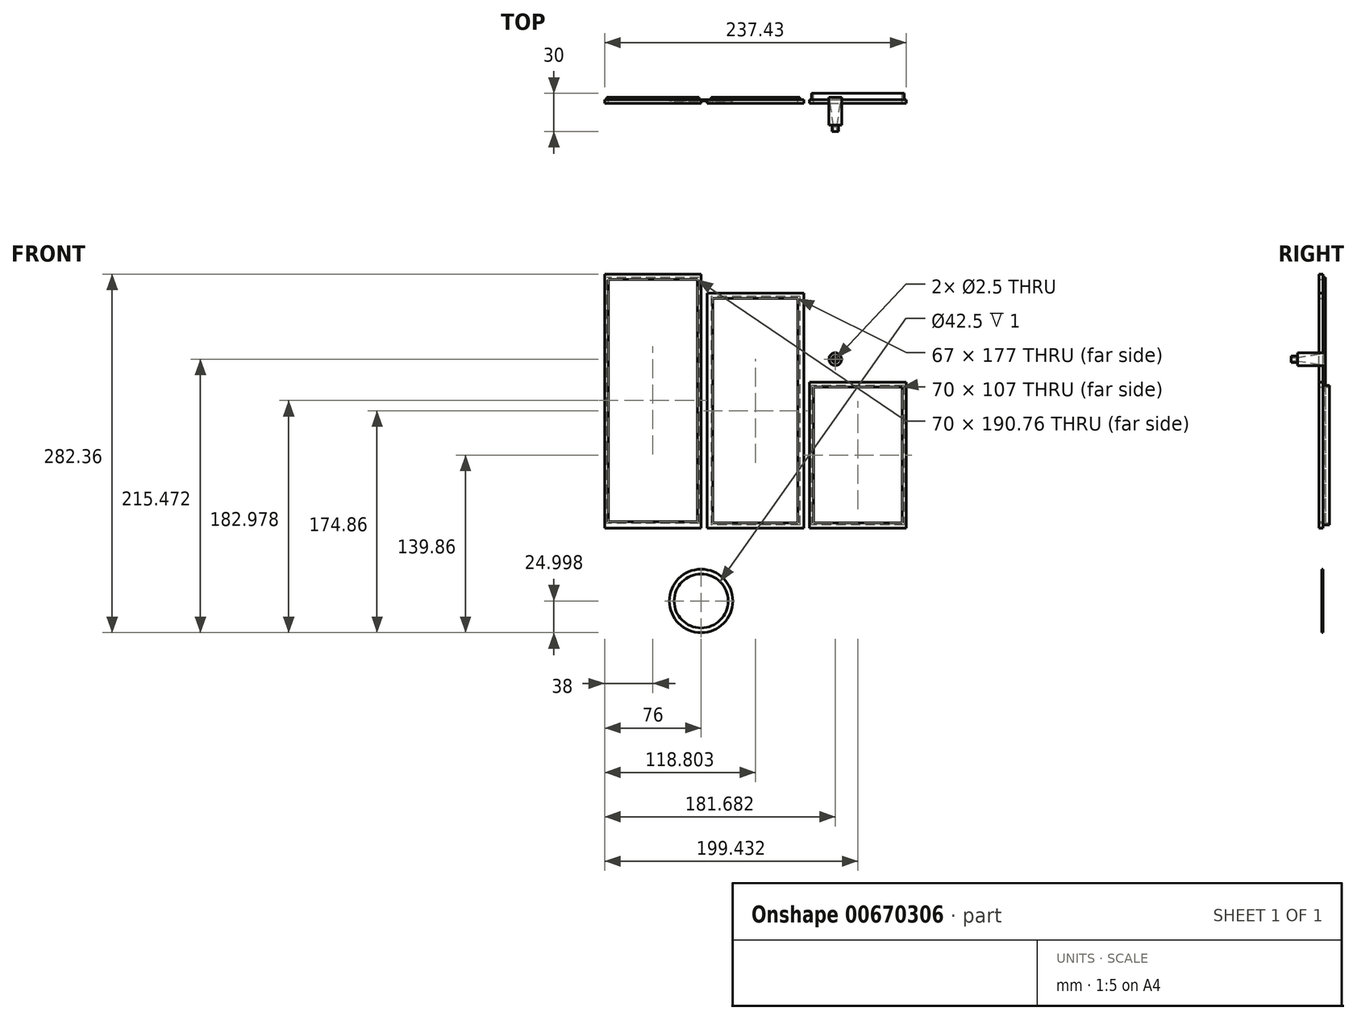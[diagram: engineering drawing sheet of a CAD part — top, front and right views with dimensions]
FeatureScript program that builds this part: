
annotation { "Feature Type Name" : "Feature", "Feature Type Description" : "" }
export const myFeature = defineFeature(function(context is Context, id is Id, definition is map)
    precondition{}
    {
        {
            var Q0;
            Q0=qCreatedBy(makeId("Front.planeOp"),FACE);
            var sketch = newSketch(context, id + "F0", { "sketchPlane" : qUnion([Q0])});
            skLineSegment(sketch, "E0.bottom", {"start": v(0, 0) * mm, "end": v(-76, 0) * mm});
            skLineSegment(sketch, "E0.top", {"start": v(0, 200) * mm, "end": v(-76, 200) * mm});
            skLineSegment(sketch, "E0.left", {"start": v(0, 0) * mm, "end": v(0, 200) * mm});
            skLineSegment(sketch, "E0.right", {"start": v(-76, 0) * mm, "end": v(-76, 200) * mm});
            skSolve(sketch);
        }
        {
            var Q0;
            Q0 = qSketchRegion(id + "F0", true);
            extrude(context, id + "F1", {"entities" : qUnion([Q0]), "depth" : 3 * mm, "offsetDistance" : 25.4 * mm});
        }
        {
            var Q0;
            Q0=makeQuery(id+"F1.opExtrude","CAP_FACE",FACE,{"disambiguationData":[OSD([sQuery(id+"F0.wireOp",EDGE,"E0.bottom"),sQuery(id+"F0.wireOp",EDGE,"E0.top"),sQuery(id+"F0.wireOp",EDGE,"E0.left"),sQuery(id+"F0.wireOp",EDGE,"E0.right")])],"isStart":true});
            var sketch = newSketch(context, id + "F2", { "sketchPlane" : qUnion([Q0])});
            skLineSegment(sketch, "E1", {"start": v(0, 0) * mm, "end": v(0, 3.74) * mm});
            skLineSegment(sketch, "E2", {"start": v(0, 0) * mm, "end": v(1.5, 0) * mm});
            skLineSegment(sketch, "E3", {"start": v(76, 200) * mm, "end": v(74.5, 200) * mm});
            skLineSegment(sketch, "E4", {"start": v(74.5, 200) * mm, "end": v(74.5, 197.5) * mm});
            skLineSegment(sketch, "E5.bottom", {"start": v(1.5, 3.74) * mm, "end": v(74.5, 3.74) * mm});
            skLineSegment(sketch, "E5.top", {"start": v(1.5, 197.5) * mm, "end": v(74.5, 197.5) * mm});
            skLineSegment(sketch, "E5.left", {"start": v(1.5, 3.74) * mm, "end": v(1.5, 197.5) * mm});
            skLineSegment(sketch, "E5.right", {"start": v(74.5, 3.74) * mm, "end": v(74.5, 197.5) * mm});
            skSolve(sketch);
        }
        {
            var Q0;
            Q0 = qSketchRegion(id + "F2", true);
            extrude(context, id + "F3", {"entities" : qUnion([Q0]), "operationType" : NewBodyOperationType.ADD, "depth" : 2 * mm, "offsetDistance" : 25.4 * mm});
        }
        {
            var Q0;
            Q0=makeQuery(id+"F3.opExtrude","CAP_FACE",FACE,{"disambiguationData":[OSD([sQuery(id+"F2.wireOp",EDGE,"E5.bottom"),sQuery(id+"F2.wireOp",EDGE,"E5.top"),sQuery(id+"F2.wireOp",EDGE,"E5.left"),sQuery(id+"F2.wireOp",EDGE,"E5.right")])],"isStart":false});
            var sketch = newSketch(context, id + "F4", { "sketchPlane" : qUnion([Q0])});
            skLineSegment(sketch, "E6", {"start": v(74.5, 3.74) * mm, "end": v(73, 3.74) * mm});
            skLineSegment(sketch, "E7", {"start": v(73, 3.74) * mm, "end": v(73, 5.24) * mm});
            skLineSegment(sketch, "E8", {"start": v(1.5, 197.5) * mm, "end": v(3, 197.5) * mm});
            skLineSegment(sketch, "E9", {"start": v(3, 197.5) * mm, "end": v(3, 196) * mm});
            skLineSegment(sketch, "E10.bottom", {"start": v(3, 196) * mm, "end": v(73, 196) * mm});
            skLineSegment(sketch, "E10.top", {"start": v(3, 5.24) * mm, "end": v(73, 5.24) * mm});
            skLineSegment(sketch, "E10.left", {"start": v(3, 196) * mm, "end": v(3, 5.24) * mm});
            skLineSegment(sketch, "E10.right", {"start": v(73, 196) * mm, "end": v(73, 5.24) * mm});
            skSolve(sketch);
        }
        {
            var Q0;
            Q0 = qSketchRegion(id + "F4", true);
            extrude(context, id + "F5", {"entities" : qUnion([Q0]), "operationType" : NewBodyOperationType.REMOVE, "oppositeDirection" : true, "depth" : 25.4 * mm, "offsetDistance" : 25.4 * mm});
        }
        {
            var Q0;
            Q0=qCreatedBy(makeId("Front.planeOp"),FACE);
            var sketch = newSketch(context, id + "F6", { "sketchPlane" : qUnion([Q0])});
            skLineSegment(sketch, "E11.bottom", {"start": v(4.8, 0) * mm, "end": v(80.8, 0) * mm});
            skLineSegment(sketch, "E11.top", {"start": v(4.8, 185) * mm, "end": v(80.8, 185) * mm});
            skLineSegment(sketch, "E11.left", {"start": v(4.8, 0) * mm, "end": v(4.8, 185) * mm});
            skLineSegment(sketch, "E11.right", {"start": v(80.8, 0) * mm, "end": v(80.8, 185) * mm});
            skSolve(sketch);
        }
        {
            var Q0;
            Q0 = qSketchRegion(id + "F6", true);
            extrude(context, id + "F7", {"entities" : qUnion([Q0]), "depth" : 3 * mm, "offsetDistance" : 25.4 * mm});
        }
        {
            var Q0;
            Q0=makeQuery(id+"F7.opExtrude","CAP_FACE",FACE,{"disambiguationData":[OSD([sQuery(id+"F6.wireOp",EDGE,"E11.bottom"),sQuery(id+"F6.wireOp",EDGE,"E11.top"),sQuery(id+"F6.wireOp",EDGE,"E11.left"),sQuery(id+"F6.wireOp",EDGE,"E11.right")])],"isStart":true});
            var sketch = newSketch(context, id + "F8", { "sketchPlane" : qUnion([Q0])});
            skLineSegment(sketch, "E12.bottom", {"start": v(-4.8, 0) * mm, "end": v(-7.8, 0) * mm});
            skLineSegment(sketch, "E12.top", {"start": v(-4.8, 2.5) * mm, "end": v(-7.8, 2.5) * mm});
            skLineSegment(sketch, "E12.left", {"start": v(-4.8, 0) * mm, "end": v(-4.8, 2.5) * mm});
            skLineSegment(sketch, "E12.right", {"start": v(-7.8, 0) * mm, "end": v(-7.8, 2.5) * mm});
            skLineSegment(sketch, "E13.bottom", {"start": v(-80.8, 185) * mm, "end": v(-77.8, 185) * mm});
            skLineSegment(sketch, "E13.top", {"start": v(-80.8, 182.5) * mm, "end": v(-77.8, 182.5) * mm});
            skLineSegment(sketch, "E13.left", {"start": v(-80.8, 185) * mm, "end": v(-80.8, 182.5) * mm});
            skLineSegment(sketch, "E13.right", {"start": v(-77.8, 185) * mm, "end": v(-77.8, 182.5) * mm});
            skLineSegment(sketch, "E14.bottom", {"start": v(-77.8, 182.5) * mm, "end": v(-7.8, 182.5) * mm});
            skLineSegment(sketch, "E14.top", {"start": v(-77.8, 2.5) * mm, "end": v(-7.8, 2.5) * mm});
            skLineSegment(sketch, "E14.left", {"start": v(-77.8, 182.5) * mm, "end": v(-77.8, 2.5) * mm});
            skLineSegment(sketch, "E14.right", {"start": v(-7.8, 182.5) * mm, "end": v(-7.8, 2.5) * mm});
            skSolve(sketch);
        }
        {
            var Q0;
            Q0=makeQuery(id+"F8.imprint","IMPRINT",FACE,{"disambiguationData":[TD([[makeQuery(id+"F8.imprint","IMPRINT",EDGE,{"derivedFrom":sQuery(id+"F8.wireOp",EDGE,"E14.bottom")}),-1.0]])]});
            extrude(context, id + "F9", {"entities" : qUnion([Q0]), "operationType" : NewBodyOperationType.ADD, "depth" : 2 * mm, "offsetDistance" : 25.4 * mm});
        }
        {
            var Q0;
            Q0=makeQuery(id+"F9.opExtrude","CAP_FACE",FACE,{"disambiguationData":[OSD([sQuery(id+"F8.wireOp",EDGE,"E14.bottom"),sQuery(id+"F8.wireOp",EDGE,"E14.top"),sQuery(id+"F8.wireOp",EDGE,"E14.left"),sQuery(id+"F8.wireOp",EDGE,"E14.right")])],"isStart":false});
            var sketch = newSketch(context, id + "F10", { "sketchPlane" : qUnion([Q0])});
            skLineSegment(sketch, "E15.bottom", {"start": v(-77.8, 182.5) * mm, "end": v(-76.3, 182.5) * mm});
            skLineSegment(sketch, "E15.top", {"start": v(-77.8, 181) * mm, "end": v(-76.3, 181) * mm});
            skLineSegment(sketch, "E15.left", {"start": v(-77.8, 182.5) * mm, "end": v(-77.8, 181) * mm});
            skLineSegment(sketch, "E15.right", {"start": v(-76.3, 182.5) * mm, "end": v(-76.3, 181) * mm});
            skLineSegment(sketch, "E16.bottom", {"start": v(-7.8, 2.5) * mm, "end": v(-9.3, 2.5) * mm});
            skLineSegment(sketch, "E16.top", {"start": v(-7.8, 4) * mm, "end": v(-9.3, 4) * mm});
            skLineSegment(sketch, "E16.left", {"start": v(-7.8, 2.5) * mm, "end": v(-7.8, 4) * mm});
            skLineSegment(sketch, "E16.right", {"start": v(-9.3, 2.5) * mm, "end": v(-9.3, 4) * mm});
            skLineSegment(sketch, "E17.bottom", {"start": v(-9.3, 4) * mm, "end": v(-76.3, 4) * mm});
            skLineSegment(sketch, "E17.top", {"start": v(-9.3, 181) * mm, "end": v(-76.3, 181) * mm});
            skLineSegment(sketch, "E17.left", {"start": v(-9.3, 4) * mm, "end": v(-9.3, 181) * mm});
            skLineSegment(sketch, "E17.right", {"start": v(-76.3, 4) * mm, "end": v(-76.3, 181) * mm});
            skSolve(sketch);
        }
        {
            var Q0;
            Q0=makeQuery(id+"F10.imprint","IMPRINT",FACE,{"disambiguationData":[TD([[makeQuery(id+"F10.imprint","IMPRINT",EDGE,{"derivedFrom":sQuery(id+"F10.wireOp",EDGE,"E17.bottom")}),-1.0]])]});
            extrude(context, id + "F11", {"entities" : qUnion([Q0]), "operationType" : NewBodyOperationType.REMOVE, "oppositeDirection" : true, "depth" : 25.4 * mm, "offsetDistance" : 25.4 * mm});
        }
        {
            var Q0;
            Q0=qCreatedBy(makeId("Front.planeOp"),FACE);
            var sketch = newSketch(context, id + "F12", { "sketchPlane" : qUnion([Q0])});
            skLineSegment(sketch, "E18.bottom", {"start": v(85.43, 0) * mm, "end": v(161.43, 0) * mm});
            skLineSegment(sketch, "E18.top", {"start": v(85.43, 115) * mm, "end": v(161.43, 115) * mm});
            skLineSegment(sketch, "E18.left", {"start": v(85.43, 0) * mm, "end": v(85.43, 115) * mm});
            skLineSegment(sketch, "E18.right", {"start": v(161.43, 0) * mm, "end": v(161.43, 115) * mm});
            skSolve(sketch);
        }
        {
            var Q0;
            Q0 = qSketchRegion(id + "F12", true);
            extrude(context, id + "F13", {"entities" : qUnion([Q0]), "depth" : 3 * mm, "offsetDistance" : 25.4 * mm});
        }
        {
            var Q0;
            Q0=makeQuery(id+"F13.opExtrude","CAP_FACE",FACE,{"disambiguationData":[OSD([sQuery(id+"F12.wireOp",EDGE,"E18.bottom"),sQuery(id+"F12.wireOp",EDGE,"E18.top"),sQuery(id+"F12.wireOp",EDGE,"E18.left"),sQuery(id+"F12.wireOp",EDGE,"E18.right")])],"isStart":true});
            var sketch = newSketch(context, id + "F14", { "sketchPlane" : qUnion([Q0])});
            skLineSegment(sketch, "E19.bottom", {"start": v(-85.43, 0) * mm, "end": v(-86.93, 0) * mm});
            skLineSegment(sketch, "E19.top", {"start": v(-85.43, 2.5) * mm, "end": v(-86.93, 2.5) * mm});
            skLineSegment(sketch, "E19.left", {"start": v(-85.43, 0) * mm, "end": v(-85.43, 2.5) * mm});
            skLineSegment(sketch, "E19.right", {"start": v(-86.93, 0) * mm, "end": v(-86.93, 2.5) * mm});
            skLineSegment(sketch, "E20.bottom", {"start": v(-161.43, 115) * mm, "end": v(-159.93, 115) * mm});
            skLineSegment(sketch, "E20.top", {"start": v(-161.43, 112.5) * mm, "end": v(-159.93, 112.5) * mm});
            skLineSegment(sketch, "E20.left", {"start": v(-161.43, 115) * mm, "end": v(-161.43, 112.5) * mm});
            skLineSegment(sketch, "E20.right", {"start": v(-159.93, 115) * mm, "end": v(-159.93, 112.5) * mm});
            skLineSegment(sketch, "E21.bottom", {"start": v(-159.93, 112.5) * mm, "end": v(-86.93, 112.5) * mm});
            skLineSegment(sketch, "E21.top", {"start": v(-159.93, 2.5) * mm, "end": v(-86.93, 2.5) * mm});
            skLineSegment(sketch, "E21.left", {"start": v(-159.93, 112.5) * mm, "end": v(-159.93, 2.5) * mm});
            skLineSegment(sketch, "E21.right", {"start": v(-86.93, 112.5) * mm, "end": v(-86.93, 2.5) * mm});
            skSolve(sketch);
        }
        {
            var Q0;
            Q0=makeQuery(id+"F14.imprint","IMPRINT",FACE,{"disambiguationData":[TD([[makeQuery(id+"F14.imprint","IMPRINT",EDGE,{"derivedFrom":sQuery(id+"F14.wireOp",EDGE,"E21.bottom")}),-1.0]])]});
            extrude(context, id + "F15", {"entities" : qUnion([Q0]), "operationType" : NewBodyOperationType.ADD, "depth" : 5 * mm, "offsetDistance" : 25.4 * mm});
        }
        {
            var Q0;
            Q0=makeQuery(id+"F15.opExtrude","CAP_FACE",FACE,{"disambiguationData":[OSD([sQuery(id+"F14.wireOp",EDGE,"E21.bottom"),sQuery(id+"F14.wireOp",EDGE,"E21.top"),sQuery(id+"F14.wireOp",EDGE,"E21.left"),sQuery(id+"F14.wireOp",EDGE,"E21.right")])],"isStart":false});
            var sketch = newSketch(context, id + "F16", { "sketchPlane" : qUnion([Q0])});
            skLineSegment(sketch, "E22.bottom", {"start": v(-86.93, 2.5) * mm, "end": v(-88.43, 2.5) * mm});
            skLineSegment(sketch, "E22.top", {"start": v(-86.93, 4) * mm, "end": v(-88.43, 4) * mm});
            skLineSegment(sketch, "E22.left", {"start": v(-86.93, 2.5) * mm, "end": v(-86.93, 4) * mm});
            skLineSegment(sketch, "E22.right", {"start": v(-88.43, 2.5) * mm, "end": v(-88.43, 4) * mm});
            skLineSegment(sketch, "E23.bottom", {"start": v(-159.93, 112.5) * mm, "end": v(-158.43, 112.5) * mm});
            skLineSegment(sketch, "E23.top", {"start": v(-159.93, 111) * mm, "end": v(-158.43, 111) * mm});
            skLineSegment(sketch, "E23.left", {"start": v(-159.93, 112.5) * mm, "end": v(-159.93, 111) * mm});
            skLineSegment(sketch, "E23.right", {"start": v(-158.43, 112.5) * mm, "end": v(-158.43, 111) * mm});
            skLineSegment(sketch, "E24.bottom", {"start": v(-158.43, 111) * mm, "end": v(-88.43, 111) * mm});
            skLineSegment(sketch, "E24.top", {"start": v(-158.43, 4) * mm, "end": v(-88.43, 4) * mm});
            skLineSegment(sketch, "E24.left", {"start": v(-158.43, 111) * mm, "end": v(-158.43, 4) * mm});
            skLineSegment(sketch, "E24.right", {"start": v(-88.43, 111) * mm, "end": v(-88.43, 4) * mm});
            skSolve(sketch);
        }
        {
            var Q0;
            Q0=makeQuery(id+"F16.imprint","IMPRINT",FACE,{"disambiguationData":[TD([[makeQuery(id+"F16.imprint","IMPRINT",EDGE,{"derivedFrom":sQuery(id+"F16.wireOp",EDGE,"E24.bottom")}),-1.0]])]});
            extrude(context, id + "F17", {"entities" : qUnion([Q0]), "operationType" : NewBodyOperationType.REMOVE, "oppositeDirection" : true, "depth" : 25.4 * mm, "offsetDistance" : 25.4 * mm});
        }
        {
            var Q0;
            Q0=qCreatedBy(makeId("Front.planeOp"),FACE);
            var sketch = newSketch(context, id + "F18", { "sketchPlane" : qUnion([Q0])});
            skCircle(sketch, "E25", {"center": v(105.68, 133.11) * mm, "radius": 5 * mm});
            skSolve(sketch);
        }
        {
            var Q0;
            Q0 = qSketchRegion(id + "F18", true);
            extrude(context, id + "F19", {"entities" : qUnion([Q0]), "depth" : 20 * mm, "offsetDistance" : 25.4 * mm});
        }
        {
            var Q0;
            Q0=makeQuery(id+"F19.opExtrude","CAP_FACE",FACE,{"disambiguationData":[OSD([sQuery(id+"F18.wireOp",EDGE,"E25")])],"isStart":false});
            var sketch = newSketch(context, id + "F20", { "sketchPlane" : qUnion([Q0])});
            skCircle(sketch, "E26", {"center": v(105.68, 133.11) * mm, "radius": 2.6 * mm});
            skSolve(sketch);
        }
        {
            var Q0;
            Q0 = qSketchRegion(id + "F20", true);
            extrude(context, id + "F21", {"entities" : qUnion([Q0]), "operationType" : NewBodyOperationType.ADD, "depth" : 5 * mm, "offsetDistance" : 25.4 * mm});
        }
        {
            var Q0;
            Q0=makeQuery(id+"F19.opExtrude","CAP_FACE",FACE,{"disambiguationData":[OSD([sQuery(id+"F18.wireOp",EDGE,"E25")])],"isStart":true});
            var sketch = newSketch(context, id + "F22", { "sketchPlane" : qUnion([Q0])});
            skCircle(sketch, "E27", {"center": v(-105.68, 133.11) * mm, "radius": 4.5 * mm});
            skSolve(sketch);
        }
        {
            var Q0;
            Q0=makeQuery(id+"F21.opExtrude","CAP_FACE",FACE,{"disambiguationData":[OSD([sQuery(id+"F20.wireOp",EDGE,"E26")])],"isStart":false});
            var sketch = newSketch(context, id + "F23", { "sketchPlane" : qUnion([Q0])});
            skCircle(sketch, "E28", {"center": v(105.68, 133.11) * mm, "radius": 0.65 * mm});
            skSolve(sketch);
        }
        {
            var Q1;
            Q1=makeQuery(id+"F23.imprint","IMPRINT",FACE,{"disambiguationData":[TD([[makeQuery(id+"F23.imprint","IMPRINT",EDGE,{"derivedFrom":sQuery(id+"F23.wireOp",EDGE,"E28")}),1.0]])]});
            var Q2;
            Q2=makeQuery(id+"F22.imprint","IMPRINT",FACE,{"disambiguationData":[TD([[makeQuery(id+"F22.imprint","IMPRINT",EDGE,{"derivedFrom":sQuery(id+"F22.wireOp",EDGE,"E27")}),1.0]])]});
            loft(context, id + "F24", {"operationType" : NewBodyOperationType.REMOVE, "sheetProfilesArray" : [{ "sheetProfileEntities" : qUnion([Q1]) }, { "sheetProfileEntities" : qUnion([Q2]) }]});
        }
        {
            var Q0;
            Q0=makeQuery(id+"F19.opExtrude","CAP_FACE",FACE,{"disambiguationData":[OSD([sQuery(id+"F18.wireOp",EDGE,"E25")])],"isStart":true});
            var sketch = newSketch(context, id + "F25", { "sketchPlane" : qUnion([Q0])});
            skCircle(sketch, "E29", {"center": v(-105.68, 133.11) * mm, "radius": 5 * mm});
            skSolve(sketch);
        }
        {
            var Q0;
            Q0 = qSketchRegion(id + "F25", true);
            extrude(context, id + "F26", {"entities" : qUnion([Q0]), "operationType" : NewBodyOperationType.ADD, "depth" : 2 * mm, "offsetDistance" : 25.4 * mm});
        }
        {
            var Q0;
            Q0=makeQuery(id+"F26.opExtrude","CAP_FACE",FACE,{"disambiguationData":[OSD([sQuery(id+"F25.wireOp",EDGE,"E29")])],"isStart":false});
            var sketch = newSketch(context, id + "F27", { "sketchPlane" : qUnion([Q0])});
            skCircle(sketch, "E30", {"center": v(-105.68, 133.11) * mm, "radius": 1.25 * mm});
            skSolve(sketch);
        }
        {
            var Q0;
            Q0 = qSketchRegion(id + "F27", true);
            extrude(context, id + "F28", {"entities" : qUnion([Q0]), "operationType" : NewBodyOperationType.REMOVE, "oppositeDirection" : true, "depth" : 31 * mm, "offsetDistance" : 25.4 * mm});
        }
        {
            var Q0;
            Q0=qCreatedBy(makeId("Front.planeOp"),FACE);
            var sketch = newSketch(context, id + "F29", { "sketchPlane" : qUnion([Q0])});
            skCircle(sketch, "E31", {"center": v(0, -57.36) * mm, "radius": 25 * mm});
            skCircle(sketch, "E32", {"center": v(0, -57.36) * mm, "radius": 21.25 * mm});
            skSolve(sketch);
        }
        {
            var Q0;
            Q0 = qSketchRegion(id + "F29", true);
            extrude(context, id + "F30", {"entities" : qUnion([Q0]), "depth" : 1 * mm, "offsetDistance" : 25.4 * mm});
        }
    });
